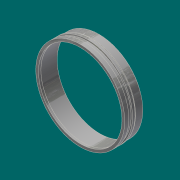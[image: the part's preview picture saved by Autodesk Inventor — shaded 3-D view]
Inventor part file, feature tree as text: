
AUTODESK INVENTOR PART (.ipt)
format: ipt  version: 2017.3 (Build 213257000, 257)  size: 204,288 bytes
history: native  units: in
note: dims shown in document units (in); Inventor stores cm internally (conversion verified against a paired STEP export)
features: revolve x1, chamfer x1, sketch x1
ambient origin geometry x8: Origin, YZ Plane, XZ Plane, XY Plane, X Axis, Y Axis, Z Axis, Center Point
bodies: Solid1 (feature_tree)
feature tree (3):
  revolve  "Revolution1"  [1 undecoded]
  chamfer  "Chamfer2"  Angle=90.0deg  [1 undecoded]
  sketch  "Sketch1"  dims[d0=17.125in d5=1.0in d6=90.0deg d13=17.75in d14=18.25in d16=1.75in d17=1.35in d18=0.0515in d19=0.0842in d20=0.0312in d21=0.125in d22=45.0deg d32=18.0in d33=0.4375in d35=0.0625in d36=0.25in d38=8.0in d43=4.25in d44=0.5in d45=60.0deg d46=0.2577in]
note: 2 required parameter values undecoded (feature->parameter linkage not recoverable at this tier; creation-order binding heuristic only, values carry confidence <= 0.55)